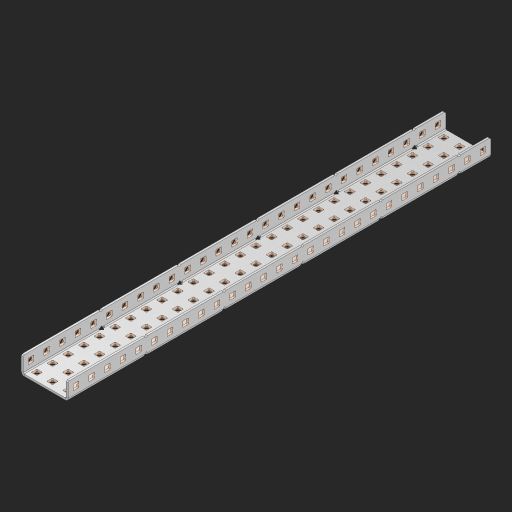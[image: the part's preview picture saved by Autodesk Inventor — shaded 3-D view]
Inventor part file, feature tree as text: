
AUTODESK INVENTOR PART (.ipt)
format: ipt  version: 2023 (Build 270158000, 158)  size: 1,692,672 bytes
history: native  units: in
note: dims shown in document units (in); Inventor stores cm internally (conversion verified against a paired STEP export)
features: other x140, extrude x134, sheet_metal_op x10, sketch x8, mirror x1, pattern_linear x1, chamfer x1
ambient origin geometry x8: Origin, YZ Plane, XZ Plane, XY Plane, X Axis, Y Axis, Z Axis, Center Point
bodies: Solid1 (feature_tree), Body (feature_tree)
feature tree (295):
  other  "Flange Pattern Plane"
  sheet_metal_op  "Flange Pattern"
  sheet_metal_op  "Body Pattern"
  other  "Arc Length"
  mirror  "Notch Mirror"
  pattern_linear  "Notch Pattern"  Spacing1=0.25in  [1 undecoded]
  chamfer  "End Chamfer"
  extrude  "Half Cut"  Depth=0.0625in
  sketch  "Sketch1"  dims[d0=1.5in]
  other  "Plate1"
  sketch  "Sketch2"  dims[d1=13.5in]
  other  "Plate2"
  sheet_metal_op  "Bend1"
  sheet_metal_op  "Corner1"
  sketch  "Sketch3"  dims[d2=0.0625in]
  other  "Flange Pattern Sketch"
  sketch  "Sketch7"  dims[d3=0.0625in]
  other  "Srf1"
  other  "Srf2"
  sketch  "Sketch8"  dims[d4=0.0312in]
  sketch  "Sketch9"  dims[d5=0.125in]
  other  "Srf91"
  sheet_metal_op  "Body Pattern Sketch"
  other  "Srf92"
  sketch  "Sketch13"  dims[d6=0.0625in]
  sketch  "Sketch14"  dims[d7=0.5in d8=90.0deg d9=0.0312in d10=0.25in d11=0.0625in d12=0.0625in d16=0.182in d17=0.02in d18=0.0625in d19=0.0in d20=0.25in d21=0.25in d46=0.172in d47=1.0in d48=0.0in d49=0.182in d50=0.02in d51=0.25in d52=0.25in d53=0.0625in d54=0.0in d55=0.172in d56=1.0in d57=0.0in d60=10.6299in d62=0.5in d63=1.1811in d65=0.5in d85=0.1473in d86=0.1782in d88=0.04in d89=0.0625in d90=0.0in d91=0.04in d92=0.0491in d95=2.5in d96=0.04in d97=0.25in d98=45.0deg d101=0.0in d102=2.497in d131=1.5in d132=10.6299in d134=0.5in d139=0.5in]
  other  "Srf856"
  other  "Srf1310"
  other  "Srf1311"
  other  "Srf1312"
  other  "Srf1376"
  other  "Srf1377"
  other  "Srf1728"
  other  "Srf1755"
  other  "Srf1878"
  other  "Srf1879"
  other  "Srf1880"
  other  "Srf1881"
  other  "Srf1882"
  other  "Srf1883"
  other  "Srf1884"
  other  "Srf1885"
  other  "Srf1886"
  other  "Srf1887"
  other  "Srf1888"
  other  "Srf1889"
  other  "Srf1890"
  other  "Srf1891"
  other  "Srf1892"
  other  "Srf1893"
  other  "Srf1894"
  other  "Srf1895"
  other  "Srf1896"
  other  "Srf1897"
  other  "Srf1898"
  other  "Srf1899"
  other  "Srf1900"
  other  "Srf1901"
  other  "Srf1902"
  other  "Srf1903"
  other  "Srf1904"
  other  "Srf1905"
  other  "Srf1906"
  other  "Srf1907"
  other  "Srf1908"
  other  "Srf1909"
  other  "Srf1910"
  other  "Srf1911"
  other  "Srf1912"
  other  "Srf1913"
  other  "Srf1914"
  other  "Srf1915"
  other  "Srf1916"
  other  "Srf1917"
  other  "Srf1918"
  other  "Srf1919"
  other  "Srf1920"
  other  "Srf1921"
  other  "Srf1922"
  other  "Srf1923"
  other  "Srf1924"
  other  "Srf1925"
  other  "Srf1942"
  other  "Srf1943"
  other  "Srf1944"
  other  "Srf1945"
  other  "Srf1946"
  other  "Srf1947"
  other  "Srf1948"
  other  "Srf1949"
  other  "Srf1950"
  other  "Srf1951"
  other  "Srf1952"
  other  "Srf1953"
  other  "Srf1954"
  other  "Srf1955"
  other  "Srf1956"
  other  "Srf1957"
  other  "Srf1958"
  other  "Srf1959"
  other  "Srf1960"
  other  "Srf1961"
  other  "Srf1962"
  other  "Srf1963"
  other  "Srf1964"
  other  "Srf1965"
  other  "Srf1966"
  other  "Srf1967"
  other  "Srf1968"
  other  "Srf1969"
  other  "Srf1970"
  other  "Srf1971"
  other  "Srf1972"
  other  "Srf1973"
  other  "Srf1974"
  other  "Srf1975"
  other  "Srf1976"
  other  "Srf1977"
  other  "Srf1978"
  other  "Srf1979"
  other  "Srf1980"
  other  "Srf1981"
  other  "Srf1982"
  other  "Srf1983"
  other  "Srf1984"
  other  "Srf1985"
  other  "Srf1986"
  other  "Srf1987"
  other  "Srf1988"
  other  "Srf1989"
  other  "Srf1990"
  other  "Srf1991"
  other  "Srf1992"
  other  "Srf1993"
  other  "Srf1994"
  other  "Srf1995"
  other  "Srf1996"
  other  "Srf1997"
  other  "Srf1998"
  other  "Srf1999"
  other  "Srf2000"
  other  "Srf2001"
  other  "Srf2002"
  other  "Srf2003"
  other  "Srf2004"
  other  "Srf2005"
  other  "Srf2006"
  other  "Srf2007"
  other  "Srf2008"
  other  "Srf2009"
  other  "Srf2010"
  other  "Srf2011"
  other  "Srf2012"
  other  "Srf2013"
  other  "Srf2014"
  other  "Srf2015"
  other  "Srf2016"
  sheet_metal_op  "Flange Stamp"
  sheet_metal_op  "Flange Circle"
  sheet_metal_op  "Body Stamp"
  sheet_metal_op  "Body Circle"
  sheet_metal_op  "Notch"
  extrude  "ExtrusionSrf2"  Depth=0.0625in
  extrude  "ExtrusionSrf92"  Depth=1.5in
  extrude  "ExtrusionSrf856"  Depth=0.02in
  extrude  "ExtrusionSrf1310"  Depth=0.0625in
  extrude  "ExtrusionSrf1311"  TaperAngle=0.0deg  [1 undecoded]
  extrude  "ExtrusionSrf1312"  Depth=0.25in
  extrude  "ExtrusionSrf1376"  Depth=0.25in
  extrude  "ExtrusionSrf1377"  Depth=1.5in
  extrude  "ExtrusionSrf1728"  Depth=1.5in TaperAngle=0.0deg
  extrude  "ExtrusionSrf1755"  Depth=1.5in
  extrude  "ExtrusionSrf1878"  Depth=0.02in
  extrude  "ExtrusionSrf1879"  Depth=0.25in
  extrude  "ExtrusionSrf1880"  Depth=0.25in
  extrude  "ExtrusionSrf1881"  Depth=0.0625in
  extrude  "ExtrusionSrf1882"  TaperAngle=0.0deg  [1 undecoded]
  extrude  "ExtrusionSrf1883"  Depth=1.5in
  extrude  "ExtrusionSrf1884"  Depth=1.5in TaperAngle=0.0deg
  extrude  "ExtrusionSrf1885"  Depth=1.5in
  extrude  "ExtrusionSrf1886"  Depth=1.5in
  extrude  "ExtrusionSrf1887"  Depth=1.5in
  extrude  "ExtrusionSrf1888"  Depth=1.5in
  extrude  "ExtrusionSrf1889"  Depth=1.5in
  extrude  "ExtrusionSrf1890"  Depth=0.0625in
  extrude  "ExtrusionSrf1891"  TaperAngle=0.0deg  [1 undecoded]
  extrude  "ExtrusionSrf1892"  Depth=1.5in
  extrude  "ExtrusionSrf1893"  Depth=1.5in
  extrude  "ExtrusionSrf1894"  Depth=1.5in
  extrude  "ExtrusionSrf1895"  Depth=0.25in TaperAngle=45.0deg
  extrude  "ExtrusionSrf1896"  TaperAngle=0.0deg  [1 undecoded]
  extrude  "ExtrusionSrf1897"  Depth=1.5in
  extrude  "ExtrusionSrf1898"  Depth=1.5in
  extrude  "ExtrusionSrf1899"  Depth=1.5in
  extrude  "ExtrusionSrf1900"  Depth=1.5in
  extrude  "ExtrusionSrf1901"  Depth=1.5in
  extrude  "ExtrusionSrf1902"  [1 undecoded]
  extrude  "ExtrusionSrf1903"  [1 undecoded]
  extrude  "ExtrusionSrf1904"  [1 undecoded]
  extrude  "ExtrusionSrf1905"  [1 undecoded]
  extrude  "ExtrusionSrf1906"  [1 undecoded]
  extrude  "ExtrusionSrf1907"  [1 undecoded]
  extrude  "ExtrusionSrf1908"  [1 undecoded]
  extrude  "ExtrusionSrf1909"  [1 undecoded]
  extrude  "ExtrusionSrf1910"  [1 undecoded]
  extrude  "ExtrusionSrf1911"  [1 undecoded]
  extrude  "ExtrusionSrf1912"  [1 undecoded]
  extrude  "ExtrusionSrf1913"  [1 undecoded]
  extrude  "ExtrusionSrf1914"  [1 undecoded]
  extrude  "ExtrusionSrf1915"  [1 undecoded]
  extrude  "ExtrusionSrf1916"  [1 undecoded]
  extrude  "ExtrusionSrf1917"  [1 undecoded]
  extrude  "ExtrusionSrf1918"  [1 undecoded]
  extrude  "ExtrusionSrf1919"  [1 undecoded]
  extrude  "ExtrusionSrf1920"  [1 undecoded]
  extrude  "ExtrusionSrf1921"  [1 undecoded]
  extrude  "ExtrusionSrf1922"  [1 undecoded]
  extrude  "ExtrusionSrf1923"  [1 undecoded]
  extrude  "ExtrusionSrf1924"  [1 undecoded]
  extrude  "ExtrusionSrf1925"  [1 undecoded]
  extrude  "ExtrusionSrf1942"  [1 undecoded]
  extrude  "ExtrusionSrf1943"  [1 undecoded]
  extrude  "ExtrusionSrf1944"  [1 undecoded]
  extrude  "ExtrusionSrf1945"  [1 undecoded]
  extrude  "ExtrusionSrf1946"  [1 undecoded]
  extrude  "ExtrusionSrf1947"  [1 undecoded]
  extrude  "ExtrusionSrf1948"  [1 undecoded]
  extrude  "ExtrusionSrf1949"  [1 undecoded]
  extrude  "ExtrusionSrf1950"  [1 undecoded]
  extrude  "ExtrusionSrf1951"  [1 undecoded]
  extrude  "ExtrusionSrf1952"  [1 undecoded]
  extrude  "ExtrusionSrf1953"  [1 undecoded]
  extrude  "ExtrusionSrf1954"  [1 undecoded]
  extrude  "ExtrusionSrf1955"  [1 undecoded]
  extrude  "ExtrusionSrf1956"  [1 undecoded]
  extrude  "ExtrusionSrf1957"  [1 undecoded]
  extrude  "ExtrusionSrf1958"  [1 undecoded]
  extrude  "ExtrusionSrf1959"  [1 undecoded]
  extrude  "ExtrusionSrf1960"  [1 undecoded]
  extrude  "ExtrusionSrf1961"  [1 undecoded]
  extrude  "ExtrusionSrf1962"  [1 undecoded]
  extrude  "ExtrusionSrf1963"  [1 undecoded]
  extrude  "ExtrusionSrf1964"  [1 undecoded]
  extrude  "ExtrusionSrf1965"  [1 undecoded]
  extrude  "ExtrusionSrf1966"  [1 undecoded]
  extrude  "ExtrusionSrf1967"  [1 undecoded]
  extrude  "ExtrusionSrf1968"  [1 undecoded]
  extrude  "ExtrusionSrf1969"  [1 undecoded]
  extrude  "ExtrusionSrf1970"  [1 undecoded]
  extrude  "ExtrusionSrf1971"  [1 undecoded]
  extrude  "ExtrusionSrf1972"  [1 undecoded]
  extrude  "ExtrusionSrf1973"  [1 undecoded]
  extrude  "ExtrusionSrf1974"  [1 undecoded]
  extrude  "ExtrusionSrf1975"  [1 undecoded]
  extrude  "ExtrusionSrf1976"  [1 undecoded]
  extrude  "ExtrusionSrf1977"  [1 undecoded]
  extrude  "ExtrusionSrf1978"  [1 undecoded]
  extrude  "ExtrusionSrf1979"  [1 undecoded]
  extrude  "ExtrusionSrf1980"  [1 undecoded]
  extrude  "ExtrusionSrf1981"  [1 undecoded]
  extrude  "ExtrusionSrf1982"  [1 undecoded]
  extrude  "ExtrusionSrf1983"  [1 undecoded]
  extrude  "ExtrusionSrf1984"  [1 undecoded]
  extrude  "ExtrusionSrf1985"  [1 undecoded]
  extrude  "ExtrusionSrf1986"  [1 undecoded]
  extrude  "ExtrusionSrf1987"  [1 undecoded]
  extrude  "ExtrusionSrf1988"  [1 undecoded]
  extrude  "ExtrusionSrf1989"  [1 undecoded]
  extrude  "ExtrusionSrf1990"  [1 undecoded]
  extrude  "ExtrusionSrf1991"  [1 undecoded]
  extrude  "ExtrusionSrf1992"  [1 undecoded]
  extrude  "ExtrusionSrf1993"  [1 undecoded]
  extrude  "ExtrusionSrf1994"  [1 undecoded]
  extrude  "ExtrusionSrf1995"  [1 undecoded]
  extrude  "ExtrusionSrf1996"  [1 undecoded]
  extrude  "ExtrusionSrf1997"  [1 undecoded]
  extrude  "ExtrusionSrf1998"  [1 undecoded]
  extrude  "ExtrusionSrf1999"  [1 undecoded]
  extrude  "ExtrusionSrf2000"  [1 undecoded]
  extrude  "ExtrusionSrf2001"  [1 undecoded]
  extrude  "ExtrusionSrf2002"  [1 undecoded]
  extrude  "ExtrusionSrf2003"  [1 undecoded]
  extrude  "ExtrusionSrf2004"  [1 undecoded]
  extrude  "ExtrusionSrf2005"  [1 undecoded]
  extrude  "ExtrusionSrf2006"  [1 undecoded]
  extrude  "ExtrusionSrf2007"  [1 undecoded]
  extrude  "ExtrusionSrf2008"  [1 undecoded]
  extrude  "ExtrusionSrf2009"  [1 undecoded]
  extrude  "ExtrusionSrf2010"  [1 undecoded]
  extrude  "ExtrusionSrf2011"  [1 undecoded]
  extrude  "ExtrusionSrf2012"  [1 undecoded]
  extrude  "ExtrusionSrf2013"  [1 undecoded]
  extrude  "ExtrusionSrf2014"  [1 undecoded]
  extrude  "ExtrusionSrf2015"  [1 undecoded]
  extrude  "ExtrusionSrf2016"  [1 undecoded]
note: 104 required parameter values undecoded (feature->parameter linkage not recoverable at this tier; creation-order binding heuristic only, values carry confidence <= 0.55)
